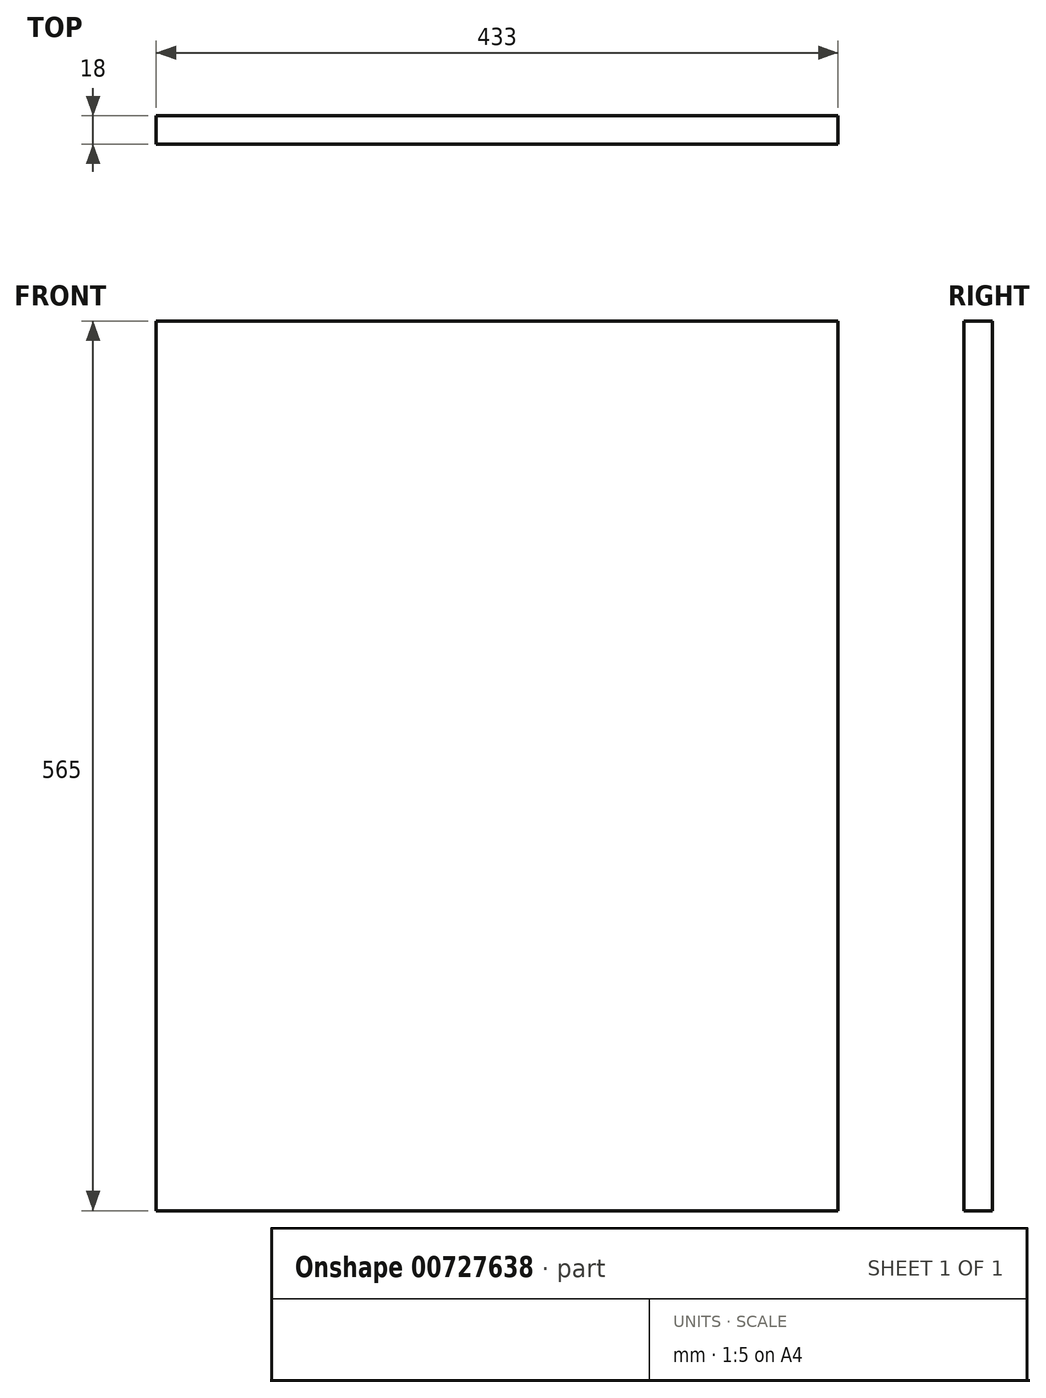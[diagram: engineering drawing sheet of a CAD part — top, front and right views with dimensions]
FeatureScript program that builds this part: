
annotation { "Feature Type Name" : "Feature", "Feature Type Description" : "" }
export const myFeature = defineFeature(function(context is Context, id is Id, definition is map)
    precondition{}
    {
        {
            var Q0;
            Q0=qCreatedBy(makeId("Front.planeOp"),FACE);
            var sketch = newSketch(context, id + "F0", { "sketchPlane" : qUnion([Q0])});
            skLineSegment(sketch, "E0.bottom", {"start": v(-244.75, 371.48) * mm, "end": v(188.25, 371.48) * mm});
            skLineSegment(sketch, "E0.top", {"start": v(-244.75, -193.52) * mm, "end": v(188.25, -193.52) * mm});
            skLineSegment(sketch, "E0.left", {"start": v(-244.75, 371.48) * mm, "end": v(-244.75, -193.52) * mm});
            skLineSegment(sketch, "E0.right", {"start": v(188.25, 371.48) * mm, "end": v(188.25, -193.52) * mm});
            skSolve(sketch);
        }
        {
            var Q0;
            Q0 = qSketchRegion(id + "F0", true);
            extrude(context, id + "F1", {"entities" : qUnion([Q0]), "oppositeDirection" : true, "depth" : 18 * mm, "offsetDistance" : 25 * mm});
        }
    });
